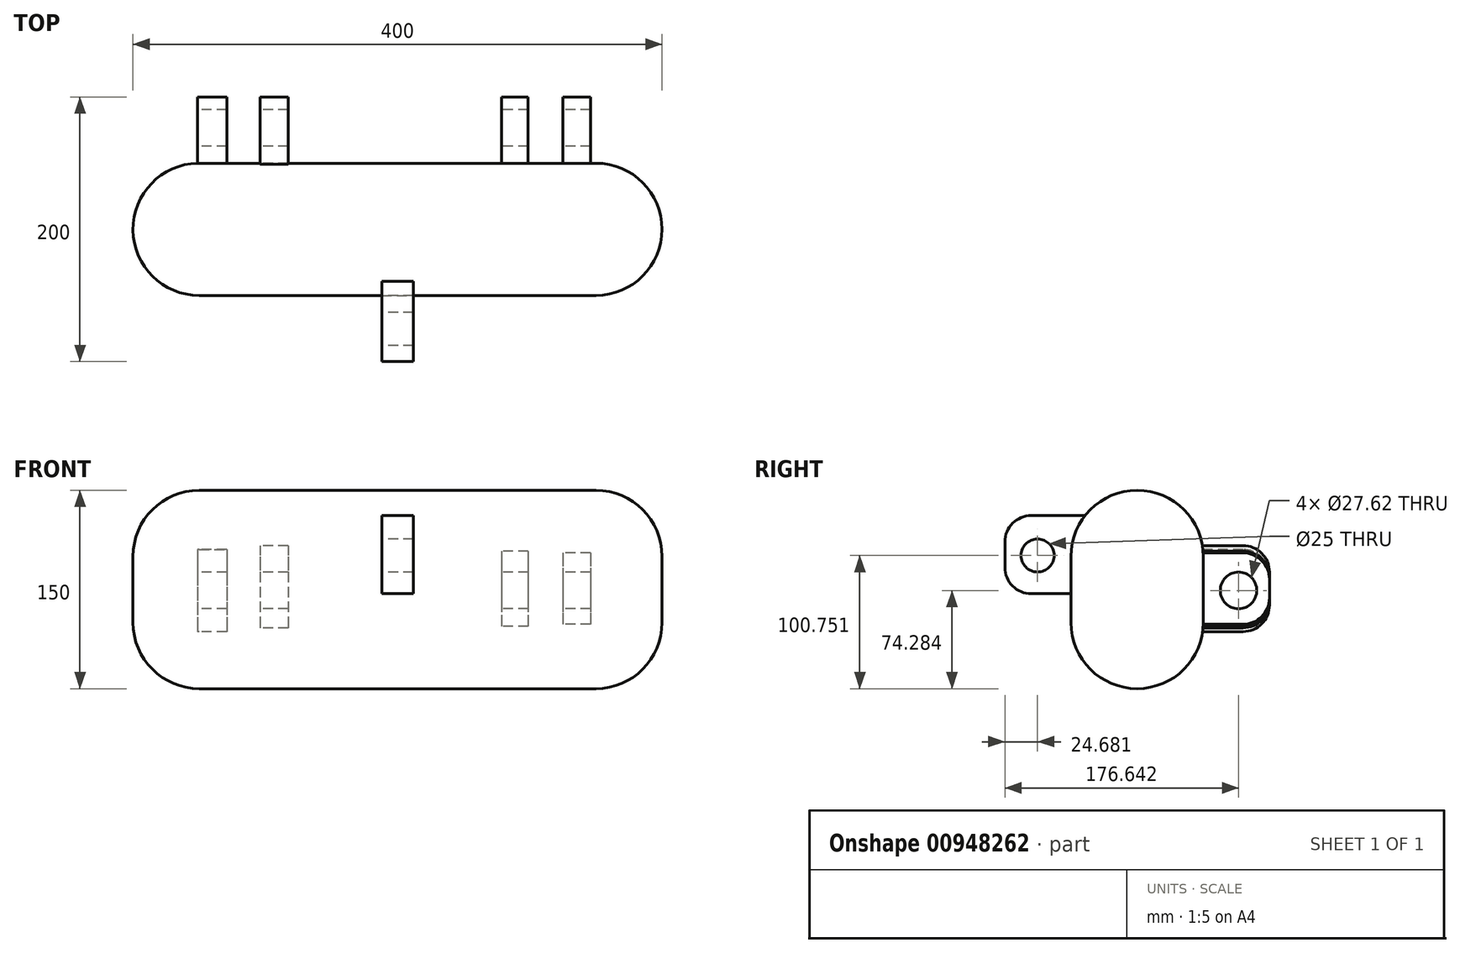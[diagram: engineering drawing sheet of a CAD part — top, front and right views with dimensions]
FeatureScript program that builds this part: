
annotation { "Feature Type Name" : "Feature", "Feature Type Description" : "" }
export const myFeature = defineFeature(function(context is Context, id is Id, definition is map)
    precondition{}
    {
        {
            var Q0;
            Q0=qCreatedBy(makeId("Top.planeOp"),FACE);
            var sketch = newSketch(context, id + "F0", { "sketchPlane" : qUnion([Q0])});
            skLineSegment(sketch, "E0.bottom", {"start": v(-200, -50) * mm, "end": v(200, -50) * mm});
            skLineSegment(sketch, "E0.top", {"start": v(-200, 50) * mm, "end": v(200, 50) * mm});
            skLineSegment(sketch, "E0.left", {"start": v(-200, -50) * mm, "end": v(-200, 50) * mm});
            skLineSegment(sketch, "E0.right", {"start": v(200, -50) * mm, "end": v(200, 50) * mm});
            skPoint(sketch, "E0.middle", {"position": v(0, 0) * mm});
            skSolve(sketch);
        }
        {
            var Q0;
            Q0=makeQuery(id+"F0.imprint","IMPRINT",FACE,{"disambiguationData":[TD([[makeQuery(id+"F0.imprint","IMPRINT",EDGE,{"derivedFrom":sQuery(id+"F0.wireOp",EDGE,"E0.bottom")}),1.0]])]});
            extrude(context, id + "F1", {"entities" : qUnion([Q0]), "depth" : 150 * mm, "offsetDistance" : 25 * mm});
        }
        {
            var Q0;
            Q0=makeQuery(id+"F1.opExtrude","SWEPT_FACE",FACE,{"disambiguationData":[OSD([sQuery(id+"F0.wireOp",EDGE,"E0.top")])]});
            var sketch = newSketch(context, id + "F2", { "sketchPlane" : qUnion([Q0])});
            skLineSegment(sketch, "E1.bottom", {"start": v(129.12, 105.4) * mm, "end": v(151.2, 105.4) * mm});
            skLineSegment(sketch, "E1.top", {"start": v(129.12, 43.17) * mm, "end": v(151.2, 43.17) * mm});
            skLineSegment(sketch, "E1.left", {"start": v(129.12, 105.4) * mm, "end": v(129.12, 43.17) * mm});
            skLineSegment(sketch, "E1.right", {"start": v(151.2, 105.4) * mm, "end": v(151.2, 43.17) * mm});
            skPoint(sketch, "E1.middle", {"position": v(140.16, 74.28) * mm});
            skLineSegment(sketch, "E2.bottom", {"start": v(82.68, 108.23) * mm, "end": v(103.83, 108.23) * mm});
            skLineSegment(sketch, "E2.top", {"start": v(82.68, 46) * mm, "end": v(103.83, 46) * mm});
            skLineSegment(sketch, "E2.left", {"start": v(82.68, 108.23) * mm, "end": v(82.68, 46) * mm});
            skLineSegment(sketch, "E2.right", {"start": v(103.83, 108.23) * mm, "end": v(103.83, 46) * mm});
            skPoint(sketch, "E2.middle", {"position": v(93.25, 77.1) * mm});
            skLineSegment(sketch, "E3.bottom", {"start": v(-98.74, 103.98) * mm, "end": v(-78.74, 103.98) * mm});
            skLineSegment(sketch, "E3.top", {"start": v(-98.74, 47.24) * mm, "end": v(-78.74, 47.24) * mm});
            skLineSegment(sketch, "E3.left", {"start": v(-98.74, 103.98) * mm, "end": v(-98.74, 47.24) * mm});
            skLineSegment(sketch, "E3.right", {"start": v(-78.74, 103.98) * mm, "end": v(-78.74, 47.24) * mm});
            skPoint(sketch, "E3.middle", {"position": v(-88.74, 75.6) * mm});
            skLineSegment(sketch, "E4.bottom", {"start": v(-145.94, 102.67) * mm, "end": v(-125.13, 102.67) * mm});
            skLineSegment(sketch, "E4.top", {"start": v(-145.94, 48.69) * mm, "end": v(-125.13, 48.69) * mm});
            skLineSegment(sketch, "E4.left", {"start": v(-145.94, 102.67) * mm, "end": v(-145.94, 48.69) * mm});
            skLineSegment(sketch, "E4.right", {"start": v(-125.13, 102.67) * mm, "end": v(-125.13, 48.69) * mm});
            skPoint(sketch, "E4.middle", {"position": v(-135.53, 75.68) * mm});
            skSolve(sketch);
        }
        {
            var Q0;
            Q0=makeQuery(id+"F2.imprint","IMPRINT",FACE,{"disambiguationData":[TD([[makeQuery(id+"F2.imprint","IMPRINT",EDGE,{"derivedFrom":sQuery(id+"F2.wireOp",EDGE,"E1.bottom")}),-1.0]])]});
            var Q1;
            Q1=makeQuery(id+"F2.imprint","IMPRINT",FACE,{"disambiguationData":[TD([[makeQuery(id+"F2.imprint","IMPRINT",EDGE,{"derivedFrom":sQuery(id+"F2.wireOp",EDGE,"E2.bottom")}),-1.0]])]});
            var Q2;
            Q2=makeQuery(id+"F2.imprint","IMPRINT",FACE,{"disambiguationData":[TD([[makeQuery(id+"F2.imprint","IMPRINT",EDGE,{"derivedFrom":sQuery(id+"F2.wireOp",EDGE,"E3.bottom")}),-1.0]])]});
            var Q3;
            Q3=makeQuery(id+"F2.imprint","IMPRINT",FACE,{"disambiguationData":[TD([[makeQuery(id+"F2.imprint","IMPRINT",EDGE,{"derivedFrom":sQuery(id+"F2.wireOp",EDGE,"E4.bottom")}),-1.0]])]});
            extrude(context, id + "F3", {"entities" : qUnion([Q0, Q1, Q2, Q3]), "operationType" : NewBodyOperationType.ADD, "depth" : 50 * mm, "offsetDistance" : 25 * mm});
        }
        {
            var Q0;
            Q0=makeQuery(id+"F3.opExtrude","SWEPT_FACE",FACE,{"disambiguationData":[OSD([sQuery(id+"F2.wireOp",EDGE,"E1.right")])]});
            var sketch = newSketch(context, id + "F4", { "sketchPlane" : qUnion([Q0])});
            skCircle(sketch, "E5", {"center": v(-76.64, 74.28) * mm, "radius": 13.8 * mm});
            skPoint(sketch, "E6", {"position": v(-100, 74.28) * mm});
            skSolve(sketch);
        }
        {
            var Q0;
            Q0=makeQuery(id+"F4.imprint","IMPRINT",FACE,{"disambiguationData":[TD([[makeQuery(id+"F4.imprint","IMPRINT",EDGE,{"derivedFrom":sQuery(id+"F4.wireOp",EDGE,"E5")}),1.0]])]});
            extrude(context, id + "F5", {"entities" : qUnion([Q0]), "operationType" : NewBodyOperationType.REMOVE, "endBound" : BoundingType.THROUGH_ALL, "oppositeDirection" : true, "depth" : 25 * mm, "offsetDistance" : 25 * mm});
        }
        {
            var Q0;
            Q0=makeQuery(id+"F1.opExtrude","SWEPT_FACE",FACE,{"disambiguationData":[OSD([sQuery(id+"F0.wireOp",EDGE,"E0.bottom")])]});
            var sketch = newSketch(context, id + "F6", { "sketchPlane" : qUnion([Q0])});
            skLineSegment(sketch, "E7.bottom", {"start": v(11.98, 71.77) * mm, "end": v(-11.98, 71.77) * mm});
            skLineSegment(sketch, "E7.top", {"start": v(11.98, 130.99) * mm, "end": v(-11.98, 130.99) * mm});
            skLineSegment(sketch, "E7.left", {"start": v(11.98, 71.77) * mm, "end": v(11.98, 130.99) * mm});
            skLineSegment(sketch, "E7.right", {"start": v(-11.98, 71.77) * mm, "end": v(-11.98, 130.99) * mm});
            skPoint(sketch, "E7.middle", {"position": v(0, 101.38) * mm});
            skSolve(sketch);
        }
        {
            var Q0;
            Q0=makeQuery(id+"F6.imprint","IMPRINT",FACE,{"disambiguationData":[TD([[makeQuery(id+"F6.imprint","IMPRINT",EDGE,{"derivedFrom":sQuery(id+"F6.wireOp",EDGE,"E7.bottom")}),-1.0]])]});
            extrude(context, id + "F7", {"entities" : qUnion([Q0]), "operationType" : NewBodyOperationType.ADD, "depth" : 50 * mm, "offsetDistance" : 25 * mm});
        }
        {
            var Q0;
            Q0=makeQuery(id+"F7.opExtrude","SWEPT_FACE",FACE,{"disambiguationData":[OSD([sQuery(id+"F6.wireOp",EDGE,"E7.right")])]});
            var sketch = newSketch(context, id + "F8", { "sketchPlane" : qUnion([Q0])});
            skCircle(sketch, "E8", {"center": v(75.32, 100.75) * mm, "radius": 12.5 * mm});
            skSolve(sketch);
        }
        {
            var Q0;
            Q0=makeQuery(id+"F8.imprint","IMPRINT",FACE,{"disambiguationData":[TD([[makeQuery(id+"F8.imprint","IMPRINT",EDGE,{"derivedFrom":sQuery(id+"F8.wireOp",EDGE,"E8")}),1.0]])]});
            extrude(context, id + "F9", {"entities" : qUnion([Q0]), "operationType" : NewBodyOperationType.REMOVE, "endBound" : BoundingType.THROUGH_ALL, "oppositeDirection" : true, "depth" : 25 * mm, "offsetDistance" : 25 * mm});
        }
        {
            var Q0;
            Q0=makeQuery(id+"F7.opExtrude","CAP_EDGE",EDGE,{"disambiguationData":[OSD([sQuery(id+"F6.wireOp",EDGE,"E7.bottom")])],"isStart":false});
            var Q1;
            Q1=makeQuery(id+"F7.opExtrude","CAP_EDGE",EDGE,{"disambiguationData":[OSD([sQuery(id+"F6.wireOp",EDGE,"E7.top")])],"isStart":false});
            var Q2;
            Q2=makeQuery(id+"F3.opExtrude","CAP_EDGE",EDGE,{"disambiguationData":[OSD([sQuery(id+"F2.wireOp",EDGE,"E4.bottom")])],"isStart":false});
            var Q3;
            Q3=makeQuery(id+"F3.opExtrude","CAP_EDGE",EDGE,{"disambiguationData":[OSD([sQuery(id+"F2.wireOp",EDGE,"E4.top")])],"isStart":false});
            var Q4;
            Q4=makeQuery(id+"F3.opExtrude","CAP_EDGE",EDGE,{"disambiguationData":[OSD([sQuery(id+"F2.wireOp",EDGE,"E3.top")])],"isStart":false});
            var Q5;
            Q5=makeQuery(id+"F3.opExtrude","CAP_EDGE",EDGE,{"disambiguationData":[OSD([sQuery(id+"F2.wireOp",EDGE,"E3.bottom")])],"isStart":false});
            var Q6;
            Q6=makeQuery(id+"F3.opExtrude","CAP_EDGE",EDGE,{"disambiguationData":[OSD([sQuery(id+"F2.wireOp",EDGE,"E2.bottom")])],"isStart":false});
            var Q7;
            Q7=makeQuery(id+"F3.opExtrude","CAP_EDGE",EDGE,{"disambiguationData":[OSD([sQuery(id+"F2.wireOp",EDGE,"E2.top")])],"isStart":false});
            var Q8;
            Q8=makeQuery(id+"F3.opExtrude","CAP_EDGE",EDGE,{"disambiguationData":[OSD([sQuery(id+"F2.wireOp",EDGE,"E1.top")])],"isStart":false});
            var Q9;
            Q9=makeQuery(id+"F3.opExtrude","CAP_EDGE",EDGE,{"disambiguationData":[OSD([sQuery(id+"F2.wireOp",EDGE,"E1.bottom")])],"isStart":false});
            fillet(context, id + "F10", {"entities" : qUnion([Q0, Q1, Q2, Q3, Q4, Q5, Q6, Q7, Q8, Q9]), "radius" : 20 * mm, "tangentPropagation" : true, "allowEdgeOverflow" : false});
        }
        {
            var Q0;
            Q0=makeQuery(id+"F1.opExtrude","SWEPT_EDGE",EDGE,{"disambiguationData":[OSD([sQuery(id+"F0.wireOp",EDGE,"E0.bottom"),sQuery(id+"F0.wireOp",EDGE,"E0.left")])]});
            var Q1;
            Q1=makeQuery(id+"F1.opExtrude","SWEPT_EDGE",EDGE,{"disambiguationData":[OSD([sQuery(id+"F0.wireOp",EDGE,"E0.bottom"),sQuery(id+"F0.wireOp",EDGE,"E0.right")])]});
            var Q2;
            Q2=makeQuery(id+"F1.opExtrude","SWEPT_EDGE",EDGE,{"disambiguationData":[OSD([sQuery(id+"F0.wireOp",EDGE,"E0.top"),sQuery(id+"F0.wireOp",EDGE,"E0.left")])]});
            var Q3;
            Q3=makeQuery(id+"F1.opExtrude","SWEPT_EDGE",EDGE,{"disambiguationData":[OSD([sQuery(id+"F0.wireOp",EDGE,"E0.top"),sQuery(id+"F0.wireOp",EDGE,"E0.right")])]});
            fillet(context, id + "F11", {"entities" : qUnion([Q0, Q1, Q2, Q3]), "radius" : 50 * mm, "tangentPropagation" : true, "allowEdgeOverflow" : false});
        }
        {
            var Q0;
            Q0=makeQuery(id+"F1.opExtrude","CAP_FACE",FACE,{"disambiguationData":[OSD([sQuery(id+"F0.wireOp",EDGE,"E0.bottom"),sQuery(id+"F0.wireOp",EDGE,"E0.top"),sQuery(id+"F0.wireOp",EDGE,"E0.left"),sQuery(id+"F0.wireOp",EDGE,"E0.right")])],"isStart":false});
            var Q1;
            Q1=makeQuery(id+"F1.opExtrude","CAP_FACE",FACE,{"disambiguationData":[OSD([sQuery(id+"F0.wireOp",EDGE,"E0.bottom"),sQuery(id+"F0.wireOp",EDGE,"E0.top"),sQuery(id+"F0.wireOp",EDGE,"E0.left"),sQuery(id+"F0.wireOp",EDGE,"E0.right")])],"isStart":true});
            fillet(context, id + "F12", {"entities" : qUnion([Q0, Q1]), "radius" : 50 * mm, "tangentPropagation" : true, "allowEdgeOverflow" : false});
        }
    });
